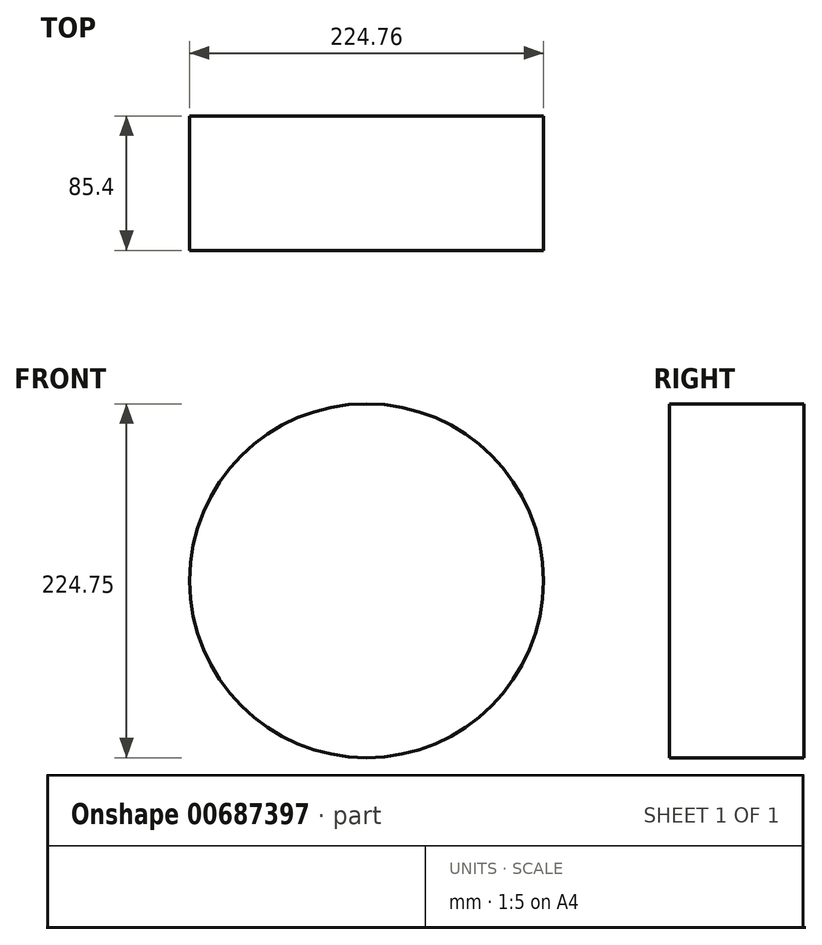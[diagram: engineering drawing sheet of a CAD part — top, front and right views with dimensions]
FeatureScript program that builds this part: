
annotation { "Feature Type Name" : "Feature", "Feature Type Description" : "" }
export const myFeature = defineFeature(function(context is Context, id is Id, definition is map)
    precondition{}
    {
        {
            var Q0;
            Q0=qCreatedBy(makeId("Front.planeOp"),FACE);
            var sketch = newSketch(context, id + "F0", { "sketchPlane" : qUnion([Q0])});
            skCircle(sketch, "E0", {"center": v(56.76, 34.73) * mm, "radius": 112.38 * mm});
            skSolve(sketch);
        }
        {
            var Q0;
            Q0=makeQuery(id+"F0.imprint","IMPRINT",FACE,{"disambiguationData":[TD([[makeQuery(id+"F0.imprint","IMPRINT",EDGE,{"derivedFrom":sQuery(id+"F0.wireOp",EDGE,"E0")}),1.0]])]});
            extrude(context, id + "F1", {"entities" : qUnion([Q0]), "depth" : 85.4 * mm, "offsetDistance" : 25 * mm});
        }
    });
